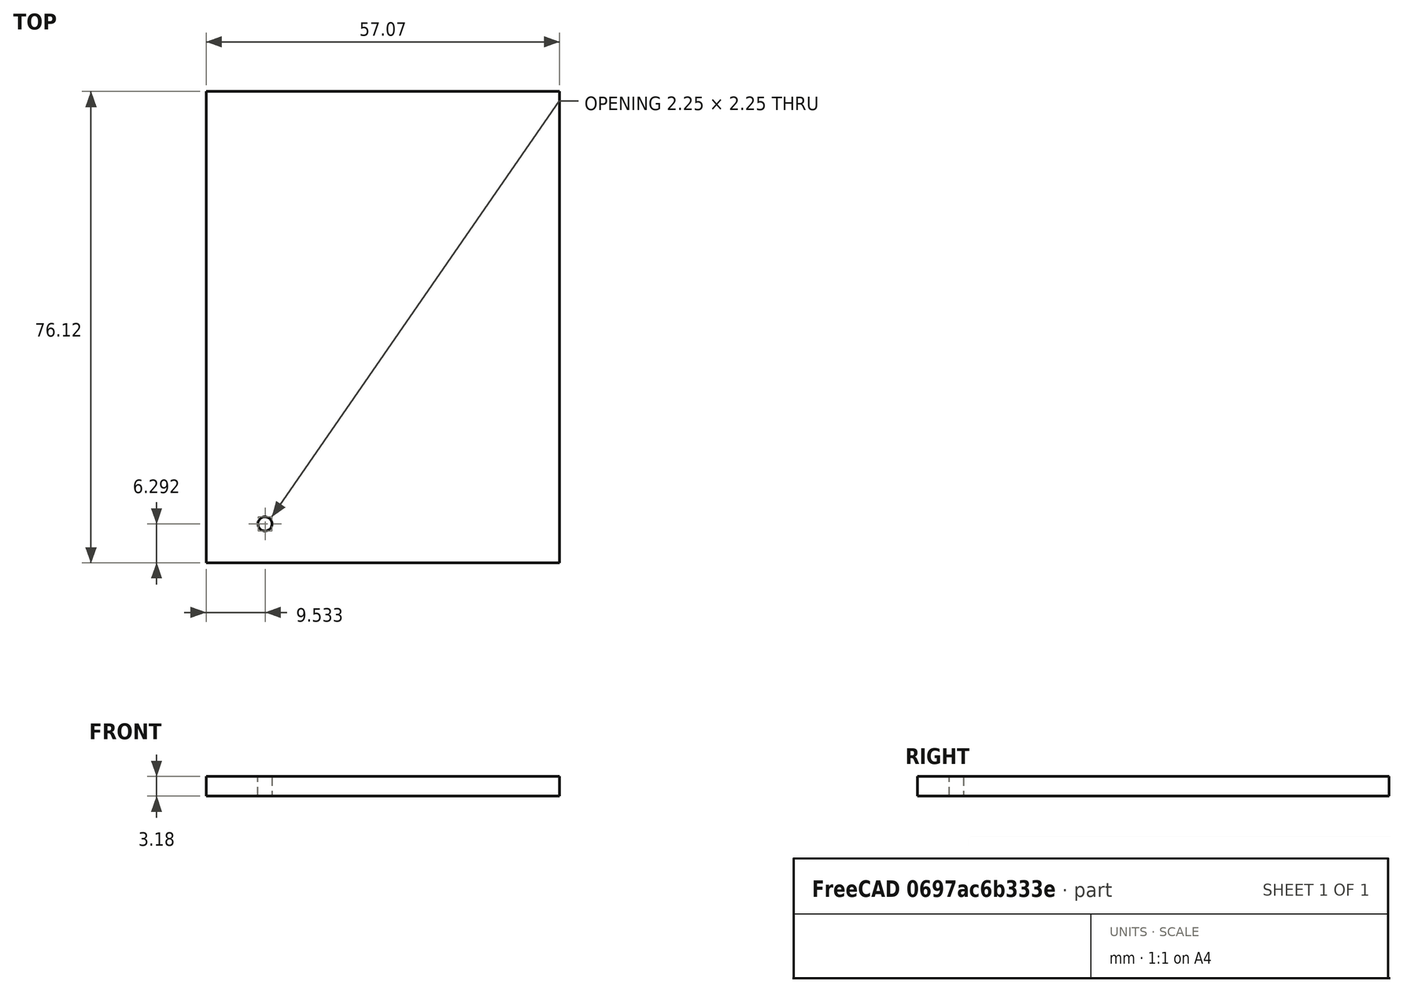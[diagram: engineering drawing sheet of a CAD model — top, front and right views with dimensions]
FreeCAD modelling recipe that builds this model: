
FCSTD DOCUMENT  (FreeCAD 0.17R13522 (Git))
Label: HFL rig wall drawing
License: All rights reserved
LicenseURL: http://en.wikipedia.org/wiki/All_rights_reserved
objects: Drawing::FeatureViewPython×6, Part::Feature×2, Part::Cut×1, Part::Extrusion×1, Drawing::FeatureViewPart×1, Drawing::FeaturePage×1
note: 4 computed .brp shape members not serialized (recipe doc carries the construction recipe); baked Part::Feature solids carry a one-line shape summary decoded from their .brp

FEATURE [Part::Feature] Face
  shape: bbox 57.07 x 76.12 x 2e-07 mm, 1 faces, 0 solids (baked)
FEATURE [Part::Feature] Face001
  shape: bbox 2.552 x 2.552 x 2e-07 mm, 1 faces, 0 solids (baked)
FEATURE [Part::Cut] Cut
  Base = -> Face
  Tool = -> Face001
FEATURE [Part::Extrusion] Extrude
  Base = -> Cut
  Dir = (0,0,-1)
  DirMode = 2
  FaceMakerClass = Part::FaceMakerBullseye
  LengthFwd = 3.175
  LengthRev = 0
  Solid = false
  Symmetric = false
FEATURE [Drawing::FeatureViewPart] Ortho  label="Ortho_0_0"
  Direction = (0,0,1)
  HiddenWidth = 0.15
  LineWidth = 0.35
  Rotation = 0
  Scale = 2
  ShowHiddenLines = false
  ShowSmoothLines = false
  Source = -> Extrude
  Tolerance = 0.05
  ViewResult = <g id="Ortho_0_0"\n   transform="rotate(0,-14.9939,-126.503) translate(-14.9939,-126.503) scale(2,2)"\n  >\n<g   fill="none"\n   stroke="rgb(0, 0, 0)"\n   stroke-linecap="butt"\n   stroke-linejoin="miter"\n   stroke-width="0.175000"\n   transform="scale(1,-1)"\n  >\n<path d="M36.46,-99.4395 L93.5339,-99.4395 " /><path d="M36.46,-175.563 L36.46,-99.4395 " /><path d="M93.5339,-99.4395 L93.5339,-175.563 " /><path d="M93.5339,-175.563 L36.46,-175.563 " /><path d="M45.9755,-168.143 C45.8005,-168.143 45.5927,-168.185 45.3945,-168.302  C45.1968,-168.417 45.0161,-168.612 44.9195,-168.849  C44.8203,-169.085 44.81,-169.351 44.8686,-169.572  C44.9261,-169.794 45.0433,-169.971 45.1673,-170.095  C45.2907,-170.219 45.4674,-170.336 45.6903,-170.393  C45.9112,-170.452 46.1772,-170.442 46.4129,-170.342  C46.6497,-170.246 46.8451,-170.065 46.9598,-169.867  C47.0769,-169.669 47.1189,-169.461 47.1185,-169.286 " /><path d="M47.1185,-169.286 C47.1222,-169.018 47.0111,-168.702 46.7837,-168.478  C46.5603,-168.251 46.2435,-168.14 45.9755,-168.143 " /></g>\n</g>
  Visible = false
  X = -14.9939
  Y = -126.503
FEATURE [Drawing::FeatureViewPython] dim001  # drawing view (typed FeaturePython)
  Rotation = 0
  ViewResult = <g> \n  <line x1="55.926100" y1="72.376000" x2="47.777562" y2="72.376000" style="stroke:rgb(0,0,255);stroke-width:0.50" />\n<line x1="55.926100" y1="224.623000" x2="47.777562" y2="224.623000" style="stroke:rgb(0,0,255);stroke-width:0.50" />\n<line x1="48.777562" y1="72.376000" x2="48.777562" y2="224.623000" style="stroke:rgb(0,0,255);stroke-width:0.50" /> \n  <polygon points="48.777562,224.623000 49.777562,221.623000 48.777562,220.623000 47.777562,221.623000" style="fill:rgb(0,0,255);stroke:rgb(0,0,255);stroke-width:0" /><polygon points="48.777562,72.376000 47.777562,75.376000 48.777562,76.376000 49.777562,75.376000" style="fill:rgb(0,0,255);stroke:rgb(0,0,255);stroke-width:0" /> \n  <text x="45.025442" y="148.930309" font-family="Verdana" font-size="5" fill="rgb(0,0,255)" text-anchor="inherit" transform="rotate(-90.000000 45.025442,148.930309)" >3</text> </g>
  Visible = false
  X = 0
  Y = 0
  arrowL1 = 3
  arrowL2 = 1
  arrowW = 2
  arrow_scheme = 0
  autoPlaceOffset = 2
  autoPlaceText = false
  click1_x = 48.7776
  click1_y = 224.261
  click2_x = 45.0254
  click2_y = 148.93
  comma_decimal_place = false
  dimension_line_overshoot = 1
  gap_datum_points = 2
  halfDimension_linear = false
  lineColor = rgb(0,0,255)
  strokeWidth = 0.5
  textFormat_linear = %(value)3.2f
  textRenderer_color = rgb(0,0,255)
  textRenderer_family = Verdana
  textRenderer_size = 5
  unit_custom_scale = 1
  unit_scheme = 2
FEATURE [Drawing::FeatureViewPython] dim002  # drawing view (typed FeaturePython)
  Rotation = 0
  ViewResult = <g> \n  <line x1="57.926100" y1="70.376000" x2="57.926100" y2="61.920169" style="stroke:rgb(0,0,255);stroke-width:0.50" />\n<line x1="172.073900" y1="70.376000" x2="172.073900" y2="61.920169" style="stroke:rgb(0,0,255);stroke-width:0.50" />\n<line x1="57.926100" y1="62.920169" x2="172.073900" y2="62.920169" style="stroke:rgb(0,0,255);stroke-width:0.50" /> \n  <polygon points="172.073900,62.920169 169.073900,61.920169 168.073900,62.920169 169.073900,63.920169" style="fill:rgb(0,0,255);stroke:rgb(0,0,255);stroke-width:0" /><polygon points="57.926100,62.920169 60.926100,63.920169 61.926100,62.920169 60.926100,61.920169" style="fill:rgb(0,0,255);stroke:rgb(0,0,255);stroke-width:0" /> \n  <text x="107.368362" y="59.456674" font-family="Verdana" font-size="5" fill="rgb(0,0,255)" text-anchor="inherit" transform="rotate(0.000000 107.368362,59.456674)" >2.25</text> </g>
  Visible = false
  X = 0
  Y = 0
  arrowL1 = 3
  arrowL2 = 1
  arrowW = 2
  arrow_scheme = 0
  autoPlaceOffset = 2
  autoPlaceText = false
  click1_x = 172.02
  click1_y = 62.9202
  click2_x = 107.368
  click2_y = 59.4567
  comma_decimal_place = false
  dimension_line_overshoot = 1
  gap_datum_points = 2
  halfDimension_linear = false
  lineColor = rgb(0,0,255)
  strokeWidth = 0.5
  textFormat_linear = %(value)3.2f
  textRenderer_color = rgb(0,0,255)
  textRenderer_family = Verdana
  textRenderer_size = 5
  unit_custom_scale = 1
  unit_scheme = 2
FEATURE [Drawing::FeatureViewPython] centerLines001  # drawing view (typed FeaturePython)
  Rotation = 0
  ViewResult = <g transform="scale(2.000000,2.000000)" stroke="rgb(0,0,255)"  stroke-width="0.150000" > <path d="M 38.480421,106.039434 L 38.480421,107.039434 M 38.480421,108.039434 L 38.480421,108.661730 "/>\n<path d="M 38.480421,106.039434 L 39.480421,106.039434 M 40.480421,106.039434 L 41.080417,106.039434 "/>\n<path d="M 38.480421,106.039434 L 38.480421,105.039434 M 38.480421,104.039434 L 38.480421,103.466266 "/>\n<path d="M 38.480421,106.039434 L 37.480421,106.039434 M 36.480421,106.039434 L 35.884952,106.039434 "/> </g> 
  Visible = false
  X = 0
  Y = 0
  centerLine_color = rgb(0,0,255)
  centerLine_len_dash = 6
  centerLine_len_dot = 2
  centerLine_len_gap = 2
  centerLine_width = 0.3
  click1_x = 82.1608
  click1_y = 217.323
  click2_x = 71.7699
  click2_y = 206.933
FEATURE [Drawing::FeatureViewPython] dim003  # drawing view (typed FeaturePython)
  Rotation = 0
  ViewResult = <g> \n  <line x1="59.926100" y1="224.623000" x2="87.993824" y2="224.623000" style="stroke:rgb(0,0,255);stroke-width:0.50" />\n<line x1="73.769904" y1="212.078868" x2="87.993824" y2="212.078868" style="stroke:rgb(0,0,255);stroke-width:0.50" />\n<line x1="86.993824" y1="224.623000" x2="86.993824" y2="212.078868" style="stroke:rgb(0,0,255);stroke-width:0.50" /> \n  <polygon points="86.993824,212.078868 85.993824,215.078868 86.993824,216.078868 87.993824,215.078868" style="fill:rgb(0,0,255);stroke:rgb(0,0,255);stroke-width:0" /><polygon points="86.993824,224.623000 87.993824,221.623000 86.993824,220.623000 85.993824,221.623000" style="fill:rgb(0,0,255);stroke:rgb(0,0,255);stroke-width:0" /> \n  <text x="93.357261" y="223.445248" font-family="Verdana" font-size="5" fill="rgb(0,0,255)" text-anchor="inherit" transform="rotate(-90.000000 93.357261,223.445248)" >0.25</text> </g>
  Visible = false
  X = 0
  Y = 0
  arrowL1 = 3
  arrowL2 = 1
  arrowW = 2
  arrow_scheme = 0
  autoPlaceOffset = 2
  autoPlaceText = false
  click1_x = 86.9938
  click1_y = 220.626
  click2_x = 93.3573
  click2_y = 223.445
  comma_decimal_place = false
  dimension_line_overshoot = 1
  gap_datum_points = 2
  halfDimension_linear = false
  lineColor = rgb(0,0,255)
  strokeWidth = 0.5
  textFormat_linear = %(value)3.2f
  textRenderer_color = rgb(0,0,255)
  textRenderer_family = Verdana
  textRenderer_size = 5
  unit_custom_scale = 1
  unit_scheme = 2
FEATURE [Drawing::FeatureViewPython] dim004  # drawing view (typed FeaturePython)
  Rotation = 0
  ViewResult = <g> \n  <line x1="76.960842" y1="204.932532" x2="76.960842" y2="199.488545" style="stroke:rgb(0,0,255);stroke-width:0.50" />\n<line x1="57.926100" y1="222.623000" x2="57.926100" y2="199.488545" style="stroke:rgb(0,0,255);stroke-width:0.50" />\n<line x1="76.960842" y1="200.488545" x2="57.926100" y2="200.488545" style="stroke:rgb(0,0,255);stroke-width:0.50" /> \n  <polygon points="57.926100,200.488545 60.926100,201.488545 61.926100,200.488545 60.926100,199.488545" style="fill:rgb(0,0,255);stroke:rgb(0,0,255);stroke-width:0" /><polygon points="76.960842,200.488545 73.960842,199.488545 72.960842,200.488545 73.960842,201.488545" style="fill:rgb(0,0,255);stroke:rgb(0,0,255);stroke-width:0" /> \n  <text x="60.009629" y="197.749850" font-family="Verdana" font-size="5" fill="rgb(0,0,255)" text-anchor="inherit" transform="rotate(0.000000 60.009629,197.749850)" >0.375</text> </g>
  Visible = false
  X = 0
  Y = 0
  arrowL1 = 3
  arrowL2 = 1
  arrowW = 2
  arrow_scheme = 0
  autoPlaceOffset = 2
  autoPlaceText = false
  click1_x = 62.5872
  click1_y = 200.489
  click2_x = 60.0096
  click2_y = 197.75
  comma_decimal_place = false
  dimension_line_overshoot = 1
  gap_datum_points = 2
  halfDimension_linear = false
  lineColor = rgb(0,0,255)
  strokeWidth = 0.5
  textFormat_linear = %(value)3.3f
  textRenderer_color = rgb(0,0,255)
  textRenderer_family = Verdana
  textRenderer_size = 5
  unit_custom_scale = 1
  unit_scheme = 2
FEATURE [Drawing::FeatureViewPython] dia001  # drawing view (typed FeaturePython)
  Rotation = 0
  ViewResult = <g>  <circle cx ="76.952074" cy ="212.071917" r="0.250000" stroke="none" fill="rgb(0,0,255)" /> \n<line x1="90.940766" y1="200.246895" x2="75.202135" y2="213.551188" style="stroke:rgb(0,0,255);stroke-width:0.50" />\n<polygon points="78.702013,210.592646 81.638680,209.419620 81.756803,208.010349 80.347531,207.892225" style="fill:rgb(0,0,255);stroke:rgb(0,0,255);stroke-width:0" />\n<polygon points="75.202135,213.551188 72.265468,214.724214 72.147345,216.133485 73.556616,216.251609" style="fill:rgb(0,0,255);stroke:rgb(0,0,255);stroke-width:0" />\n<line x1="90.940766" y1="200.246895" x2="109.064479" y2="200.246895" style="stroke:rgb(0,0,255);stroke-width:0.50" />\n<text x="92.390663" y="198.555348" font-family="Verdana" font-size="5" fill="rgb(0,0,255)" text-anchor="inherit" transform="rotate(0.000000 92.390663,198.555348)" >Ø0.09</text> </g>
  Visible = false
  X = 0
  Y = 0
  arrowL1 = 3
  arrowL2 = 1
  arrowW = 2
  arrow_scheme = 0
  autoPlaceOffset = 2
  autoPlaceText = false
  centerPointDia = 0.5
  click1_x = 90.9408
  click1_y = 200.247
  click2_x = 109.064
  click2_y = 200.247
  click3_x = 92.3907
  click3_y = 198.555
  comma_decimal_place = false
  lineColor = rgb(0,0,255)
  strokeWidth = 0.5
  textFormat_circular = Ø%(value)3.3f
  textRenderer_color = rgb(0,0,255)
  textRenderer_family = Verdana
  textRenderer_size = 5
  unit_custom_scale = 1
  unit_scheme = 2
FEATURE [Drawing::FeaturePage] Page
  EditableTexts = AUTHOR NAME | CREATION DATE | SUPERVISOR NAME | CHECK DATE | SCALE | WEIGHT | NUMBER | SHEET | TITLE | SUBTITLE
  Group = -> [Ortho,dim001,dim002,centerLines001,dim003,dim004,dia001]
  Template = C:/Program Files/FreeCAD 0.17/data/Mod/Drawing/Templates/A3_Landscape.svg
